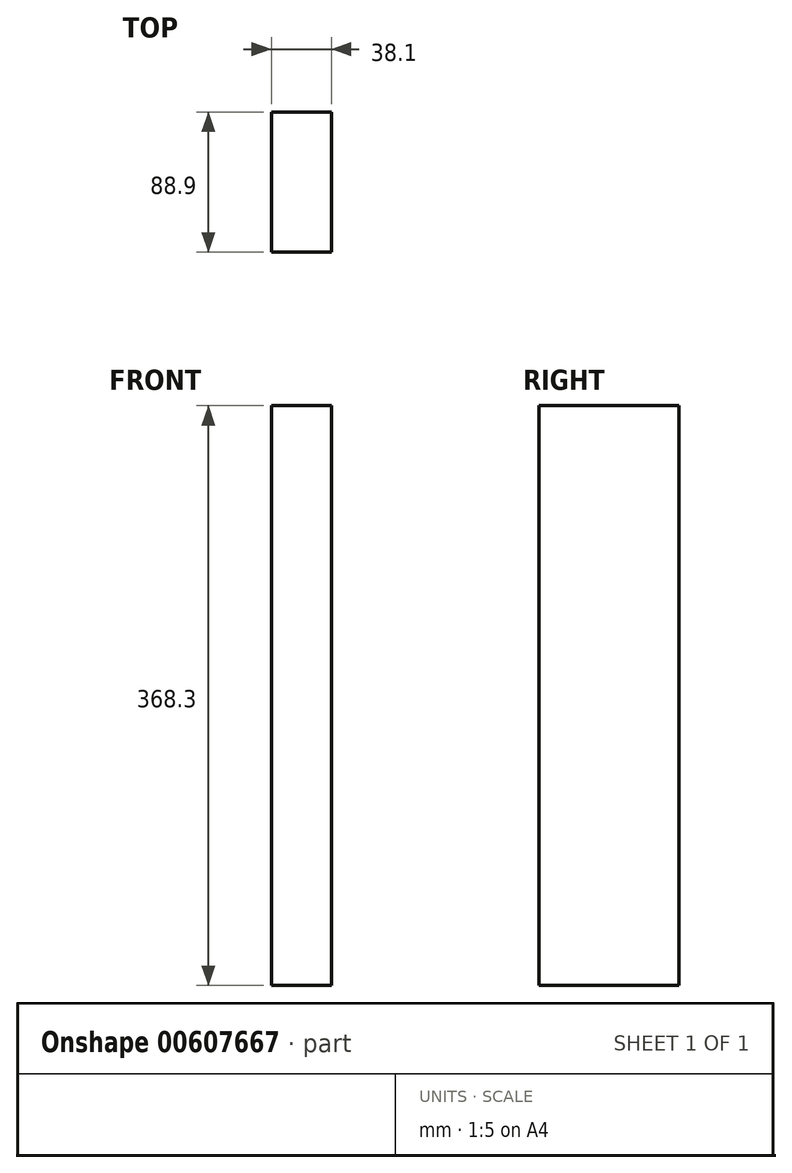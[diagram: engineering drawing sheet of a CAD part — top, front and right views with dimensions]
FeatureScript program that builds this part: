
annotation { "Feature Type Name" : "Feature", "Feature Type Description" : "" }
export const myFeature = defineFeature(function(context is Context, id is Id, definition is map)
    precondition{}
    {
        {
            var Q0;
            Q0=qCreatedBy(makeId("Front.planeOp"),FACE);
            var sketch = newSketch(context, id + "F0", { "sketchPlane" : qUnion([Q0])});
            skLineSegment(sketch, "E0", {"start": v(0, 0) * mm, "end": v(0, 63.5) * mm});
            skLineSegment(sketch, "E1", {"start": v(0, 0) * mm, "end": v(0, -304.8) * mm});
            skLineSegment(sketch, "E2", {"start": v(0, -304.8) * mm, "end": v(38.1, -304.8) * mm});
            skLineSegment(sketch, "E3.bottom", {"start": v(38.1, -304.8) * mm, "end": v(0, -304.8) * mm});
            skLineSegment(sketch, "E3.top", {"start": v(38.1, 63.5) * mm, "end": v(0, 63.5) * mm});
            skLineSegment(sketch, "E3.left", {"start": v(38.1, -304.8) * mm, "end": v(38.1, 63.5) * mm});
            skLineSegment(sketch, "E3.right", {"start": v(0, -304.8) * mm, "end": v(0, 63.5) * mm});
            skSolve(sketch);
        }
        {
            var Q0;
            Q0=qSketchRegion(id+"F0",true);
            extrude(context, id + "F1", {"entities" : qUnion([Q0]), "depth" : 88.9 * mm, "offsetDistance" : 25.4 * mm});
        }
    });
